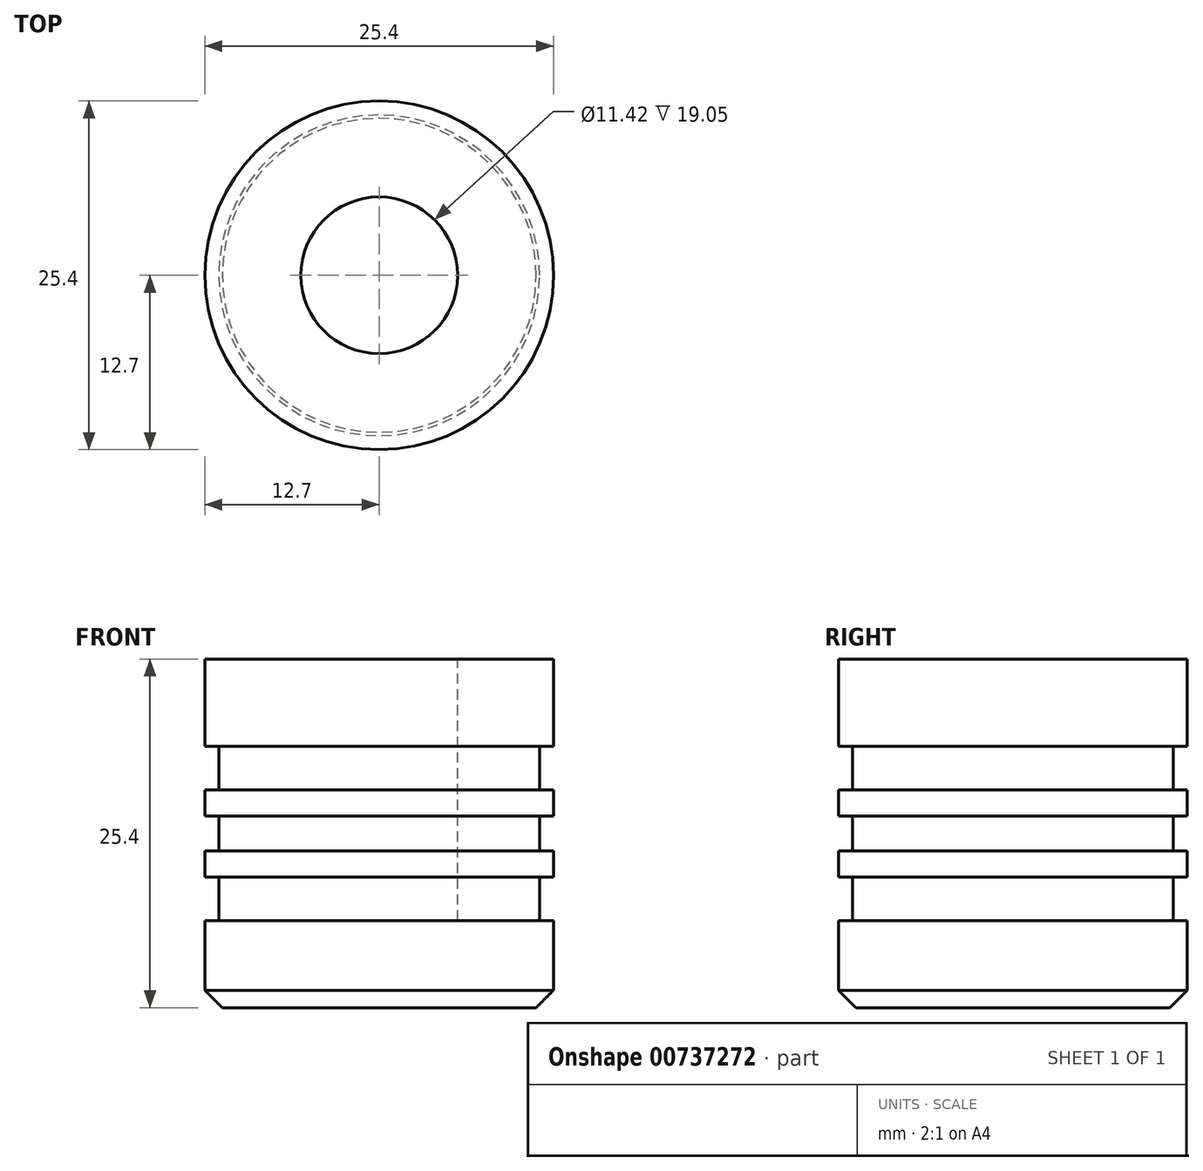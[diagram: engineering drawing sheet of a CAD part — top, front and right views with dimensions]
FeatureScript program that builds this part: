
annotation { "Feature Type Name" : "Feature", "Feature Type Description" : "" }
export const myFeature = defineFeature(function(context is Context, id is Id, definition is map)
    precondition{}
    {
        {
            var Q0;
            Q0=qCreatedBy(makeId("Top.planeOp"),FACE);
            var sketch = newSketch(context, id + "F0", { "sketchPlane" : qUnion([Q0])});
            skCircle(sketch, "E0", {"center": v(0, 0) * mm, "radius": 12.7 * mm});
            skSolve(sketch);
        }
        {
            var Q0;
            Q0=makeQuery(id+"F0.imprint","IMPRINT",FACE,{"disambiguationData":[TD([[makeQuery(id+"F0.imprint","IMPRINT",EDGE,{"derivedFrom":sQuery(id+"F0.wireOp",EDGE,"E0")}),1.0]])]});
            extrude(context, id + "F1", {"entities" : qUnion([Q0]), "depth" : 25.4 * mm});
        }
        {
            var Q0;
            Q0=makeQuery(id+"F1.opExtrude","CAP_FACE",FACE,{"disambiguationData":[OSD([sQuery(id+"F0.wireOp",EDGE,"E0")])],"isStart":false});
            var sketch = newSketch(context, id + "F2", { "sketchPlane" : qUnion([Q0])});
            skCircle(sketch, "E1", {"center": v(0, 0) * mm, "radius": 5.7 * mm});
            skSolve(sketch);
        }
        {
            var Q0;
            Q0=qSketchRegion(id+"F2",true);
            extrude(context, id + "F3", {"entities" : qUnion([Q0]), "operationType" : NewBodyOperationType.REMOVE, "oppositeDirection" : true, "depth" : 19.05 * mm});
        }
        {
            var Q0;
            Q0=makeQuery(id+"F1.opExtrude","CAP_FACE",FACE,{"disambiguationData":[OSD([sQuery(id+"F0.wireOp",EDGE,"E0")])],"isStart":false});
            cPlane(context, id + "F4", {"entities" : qUnion([Q0]), "cplaneType" : CPlaneType.OFFSET, "offset" : 12.7 * mm, "oppositeDirection" : true, "width" : 152.4 * mm, "height" : 152.4 * mm});
        }
        {
            var Q0;
            Q0=qCreatedBy(id+"F4.planeOp",FACE);
            var sketch = newSketch(context, id + "F5", { "sketchPlane" : qUnion([Q0])});
            skCircle(sketch, "E2", {"center": v(0, 0) * mm, "radius": 12.7 * mm});
            skCircle(sketch, "E3.0", {"center": v(0, 0) * mm, "radius": 11.68 * mm});
            skSolve(sketch);
        }
        {
            var Q0;
            Q0=qSketchRegion(id+"F5",true);
            extrude(context, id + "F6", {"entities" : qUnion([Q0]), "operationType" : NewBodyOperationType.REMOVE, "oppositeDirection" : true, "depth" : 6.35 * mm, "hasSecondDirection" : true, "secondDirectionOppositeDirection" : false, "secondDirectionDepth" : 6.35 * mm});
        }
        {
            var Q0;
            Q0=qSketchRegion(id+"F5",true);
            extrude(context, id + "F7", {"entities" : qUnion([Q0]), "operationType" : NewBodyOperationType.ADD, "depth" : 3.17 * mm, "hasSecondDirection" : true, "secondDirectionOppositeDirection" : true, "secondDirectionDepth" : 3.17 * mm});
        }
        {
            var Q0;
            Q0=qSketchRegion(id+"F5",true);
            extrude(context, id + "F8", {"entities" : qUnion([Q0]), "operationType" : NewBodyOperationType.REMOVE, "oppositeDirection" : true, "depth" : 1.27 * mm, "hasSecondDirection" : true, "secondDirectionOppositeDirection" : false, "secondDirectionDepth" : 1.27 * mm});
        }
        {
            var Q0;
            Q0=makeQuery(id+"F1.opExtrude","CAP_EDGE",EDGE,{"disambiguationData":[OSD([sQuery(id+"F0.wireOp",EDGE,"E0")])],"isStart":true});
            chamfer(context, id + "F9", {"entities" : qUnion([Q0]), "width" : 1.27 * mm, "tangentPropagation" : true});
        }
    });
